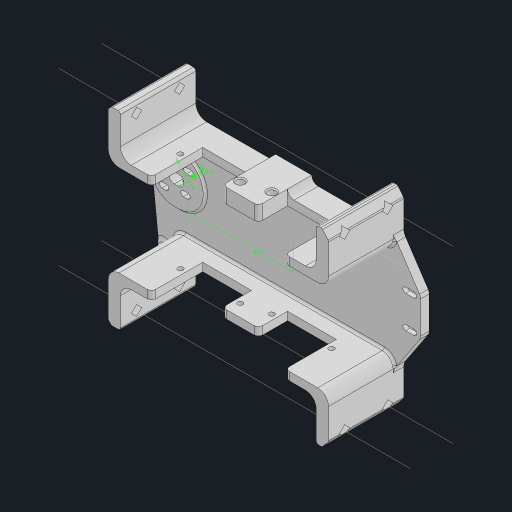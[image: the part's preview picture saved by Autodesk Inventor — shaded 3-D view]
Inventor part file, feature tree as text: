
AUTODESK INVENTOR PART (.ipt)
format: ipt  version: 2023.2 (Build 272271030, 271C)  size: 1,438,720 bytes
history: native  units: mm
features: extrude x15, sketch x15, fillet x9, projected_geometry x8, other x4, hole x1, chamfer x1
ambient origin geometry x8: Origin, YZ Plane, XZ Plane, XY Plane, X Axis, Y Axis, Z Axis, Center Point
bodies: Solid1 (feature_tree)
feature tree (53):
  extrude  "Extrusion1"  Depth=24.0mm
  extrude  "Extrusion2"  Depth=101.0mm
  extrude  "Extrusion3"  Depth=18.2mm
  extrude  "Extrusion4"  Depth=16.5mm
  other  "Work Axis7"
  other  "Work Axis8"
  other  "Work Axis9"
  other  "Work Axis10"
  extrude  "Extrusion7"  Depth=40.0mm
  hole  "Hole1"  [1 undecoded]
  extrude  "Extrusion8"  Depth=5.0mm
  extrude  "Extrusion9"  Depth=5.0mm
  extrude  "Extrusion10"  Depth=35.0mm
  fillet  "Fillet2"  Radius=3.6mm
  sketch  "Sketch15"  dims[d25=3.6mm d26=4.0mm d27=0.0mm]
  extrude  "Extrusion12"  Depth=4.0mm TaperAngle=0.0deg
  extrude  "Extrusion13"  Depth=1.5mm
  extrude  "Extrusion11"  Depth=42.4mm
  extrude  "Extrusion14"  Depth=35.0mm
  fillet  "Fillet4"  Radius=11.2mm
  extrude  "Extrusion15"  Depth=2.5mm
  fillet  "Fillet5"  Radius=27.8mm
  fillet  "Fillet6"  [1 undecoded]
  fillet  "Fillet7"  Radius=4.5mm
  fillet  "Fillet8"  Radius=16.0mm
  fillet  "Fillet9"  Radius=16.0mm
  fillet  "Fillet10"  Radius=12.0mm
  extrude  "Extrusion17"  Depth=3.0mm
  extrude  "Extrusion18"  Depth=3.0mm
  chamfer  "Chamfer1"  Distance=35.0mm
  fillet  "Fillet11"  Radius=7.5mm
  sketch  "Sketch4"  dims[d0=135.0mm d1=24.0mm]
  projected_geometry  "Projected Loop1"
  sketch  "Sketch5"  dims[d2=101.0mm d6=101.0mm]
  projected_geometry  "Projected Loop2"
  sketch  "Sketch6"  dims[d8=22.5mm d9=18.2mm]
  projected_geometry  "Projected Loop3"
  projected_geometry  "Projected Loop4"
  sketch  "Sketch9"  dims[d10=16.5mm d11=16.5mm]
  sketch  "Sketch10"  dims[d14=33.0mm d15=40.0mm]
  sketch  "Sketch11"  dims[d16=26.0mm d17=32.0mm]
  sketch  "Sketch12"  dims[d18=3.6mm d19=5.0mm]
  sketch  "Sketch13"  dims[d20=5.0mm d21=5.0mm]
  projected_geometry  "Projected Loop5"
  sketch  "Sketch14"  dims[d22=20.0mm d23=35.0mm d24=3.6mm]
  sketch  "Sketch16"  dims[d28=1.5mm d29=1.5mm]
  sketch  "Sketch17"  dims[d30=42.4mm d31=21.2mm]
  projected_geometry  "Projected Loop6"
  sketch  "Sketch18"  dims[d32=31.0mm d33=0.0mm d34=35.0mm d35=11.2mm]
  projected_geometry  "Projected Loop7"
  sketch  "Sketch21"  dims[d36=22.7mm d39=2.5mm d40=27.8mm d41=0.0mm d42=0.0mm d43=4.5mm d44=16.0mm d45=16.0mm d46=12.0mm]
  projected_geometry  "Projected Loop9"
  sketch  "Sketch22"  dims[d47=3.0mm d48=3.4mm d49=20.0mm d50=35.0mm d51=7.5mm d53=0.0mm d54=0.0mm d55=0.0mm d56=18.5mm d57=20.0mm d58=20.0mm d69=5.0mm d70=64.5mm d71=64.5mm d72=5.0mm d73=0.5mm d74=0.0mm d75=2.5mm d76=6.0mm d77=5.5mm d78=2.0mm d79=90.0deg d80=8.0mm d81=20.594885mm d84=6.0mm d85=6.0mm d86=133.604603mm d87=137.331323mm d88=0.27328mm d89=49.5mm d90=12.0mm d91=16.0mm d92=45.0deg d93=1.0mm d94=2.5mm d95=0.0mm d96=0.0mm d97=5.0mm d98=5.0mm d99=2.0mm d100=0.0mm d101=1.0mm d102=5.0mm d103=0.0mm d104=0.0mm d105=1.0mm d107=0.0mm d108=0.0mm d109=2.5mm d110=2.5mm d111=4.0mm d112=15.0mm d113=7.5mm d114=58.0mm d116=10.0mm d117=0.0mm d118=2.5mm d119=2.0mm d120=0.0mm d121=6.0mm d122=7.0mm d123=7.0mm d124=1.0mm d125=23.0mm d126=1.0mm d127=0.0mm d128=5.0mm d129=6.0mm d130=1.0mm d131=0.0mm d132=5.0mm d133=5.0mm d134=1.0mm d135=2.0mm d136=1.1mm d137=2.0mm d141=3.0mm d142=0.0mm d143=3.7mm d144=3.7mm d145=3.5mm d146=0.0mm d147=0.5mm d148=2.0mm d149=45.0deg d150=3.0mm]
note: 2 required parameter values undecoded (feature->parameter linkage not recoverable at this tier; creation-order binding heuristic only, values carry confidence <= 0.55)
